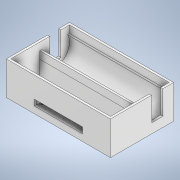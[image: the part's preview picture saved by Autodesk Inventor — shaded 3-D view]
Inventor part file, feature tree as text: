
AUTODESK INVENTOR PART (.ipt)
format: ipt  version: 2022 (Build 260153000, 153)  size: 200,192 bytes
history: native  units: mm
features: extrude x7, sketch x7, other x2, shell x1
ambient origin geometry x8: Origin, YZ Plane, XZ Plane, XY Plane, X Axis, Y Axis, Z Axis, Center Point
bodies: Solid1 (feature_tree)
feature tree (17):
  other  "Annotations"
  extrude  "Outer-Shell"  Depth=85.0mm
  shell  "Shell1"  Thickness=45.0mm
  extrude  "Battery_Holder"  Depth=3.0mm
  extrude  "Battery_Cutout"  Depth=32.0mm TaperAngle=0.0deg
  extrude  "Voltmeter_Cutouts"  Depth=20.0mm
  extrude  "Controller_Stand"  TaperAngle=0.0deg  [1 undecoded]
  extrude  "USB_Access"  Depth=32.0mm
  extrude  "M3_Mount_Holes"  TaperAngle=0.0deg  [1 undecoded]
  sketch  "Sketch1"  dims[d0=140.0mm d1=85.0mm d2=45.0mm]
  sketch  "Sketch2"  dims[d3=0.0mm d4=3.0mm]
  sketch  "Sketch3"  dims[d5=40.0mm d6=32.0mm d7=0.0mm]
  sketch  "Sketch4"  dims[d8=40.0mm d9=20.0mm]
  sketch  "Sketch5"  dims[d10=40.0mm d11=0.0mm]
  sketch  "Sketch6"  dims[d15=15.0mm d16=32.0mm]
  sketch  "Sketch7"  dims[d17=14.5mm d18=0.0mm d19=0.0mm d21=10.5mm d22=30.0mm d23=64.0mm d24=9.0mm d25=0.0mm d28=65.0mm d29=8.0mm d30=9.0mm d31=9.0mm d32=0.0mm d33=23.0mm d34=58.0mm d35=12.0mm d36=2.8mm d37=0.0mm d38=0.0mm d12=9.013876mm d13=0.986881mm d14=32.0mm]
  other  "Linear Dimension 1"
note: 2 required parameter values undecoded (feature->parameter linkage not recoverable at this tier; creation-order binding heuristic only, values carry confidence <= 0.55)
